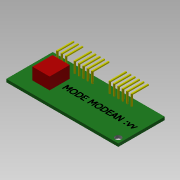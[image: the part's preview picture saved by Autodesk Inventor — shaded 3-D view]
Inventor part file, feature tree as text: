
AUTODESK INVENTOR PART (.ipt)
format: ipt  version: 2015 SP1 (Build 190203100, 203)  size: 152,576 bytes
history: native  units: mm
features: sketch x3, extrude x2, sweep x1, pattern_linear x1
ambient origin geometry x8: Origin, YZ Plane, XZ Plane, XY Plane, X Axis, Y Axis, Z Axis, Center Point
bodies: Solid1 (feature_tree)
feature tree (7):
  sketch  "Sketch1"  dims[d0=65.024mm d1=27.0mm]
  extrude  "Extrusion1"  Depth=27.0mm
  extrude  "Extrusion2"  Depth=3.5mm
  sweep  "Sweep1"
  pattern_linear  "Rectangular Pattern1"  Spacing1=3.0mm  [1 undecoded]
  sketch  "Sketch3"  dims[d4=3.0mm d5=3.0mm d6=3.0mm d7=3.0mm d8=9.96mm d9=11.66mm d10=1.0mm d11=1.27mm d12=3.937mm d13=1.7mm d14=0.0mm d15=8.62mm d16=0.0mm d17=6.15mm d18=90.0deg d19=7.87mm d20=90.0deg d21=0.0mm d22=0.0mm d23=180.0mm d25=2.54mm]
  sketch  "Sketch2"  dims[d2=3.5mm d3=3.5mm]
note: 1 required parameter value undecoded (feature->parameter linkage not recoverable at this tier; creation-order binding heuristic only, values carry confidence <= 0.55)
